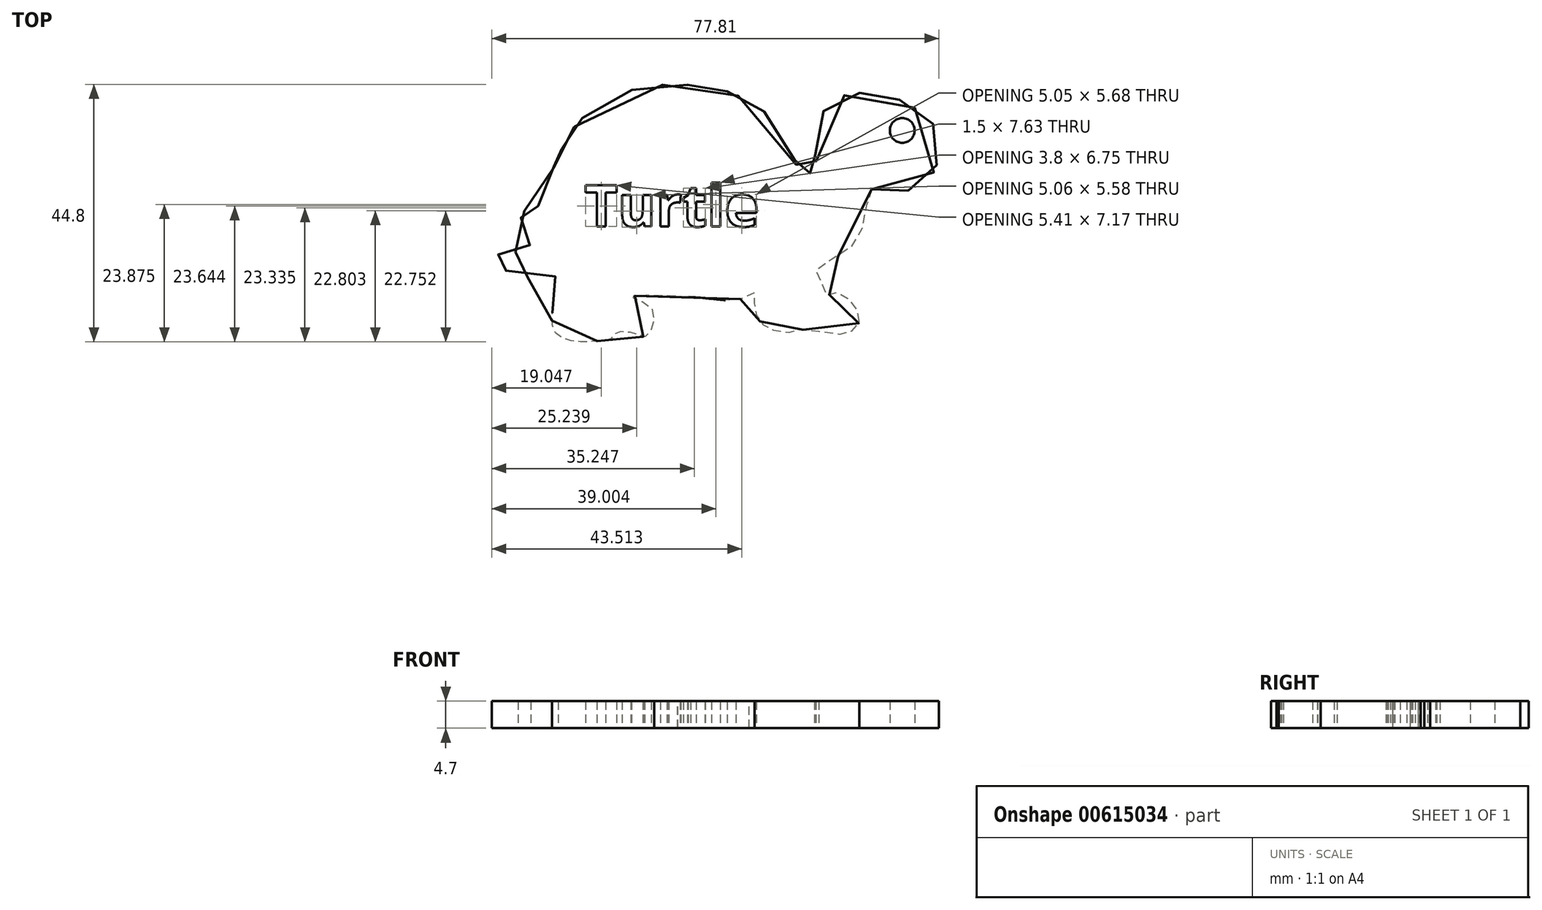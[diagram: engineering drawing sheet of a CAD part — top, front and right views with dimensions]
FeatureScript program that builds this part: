
annotation { "Feature Type Name" : "Feature", "Feature Type Description" : "" }
export const myFeature = defineFeature(function(context is Context, id is Id, definition is map)
    precondition{}
    {
        {
            var Q0;
            Q0=qCreatedBy(makeId("Top.planeOp"),FACE);
            var sketch = newSketch(context, id + "F0", { "sketchPlane" : qUnion([Q0])});
            skFitSpline(sketch, "E0", {"points": [v(-11.52, 31.86) * mm, v(-12.84, 26.48) * mm, v(-16.24, 20.92) * mm, v(-21.24, 17.52) * mm, v(-19.54, 14.32) * mm, v(-19.35, 13.47) * mm, v(-17.66, 13.94) * mm, v(-15.77, 13) * mm, v(-13.88, 10.45) * mm, v(-13.88, 8.37) * mm, v(-15.3, 7.05) * mm, v(-17.84, 6.68) * mm, v(-24.07, 7.43) * mm, v(-25.67, 6.96) * mm, v(-28.7, 7.34) * mm, v(-30.39, 8.28) * mm, v(-31.52, 9.98) * mm, v(-31.9, 12.05) * mm, v(-31.9, 13.84) * mm, v(-34.07, 12.9) * mm, v(-40.1, 12.9) * mm, v(-53.3, 13.18) * mm, v(-49.72, 11.02) * mm, v(-50.67, 6.4) * mm, v(-52.08, 6.58) * mm, v(-55.95, 6.96) * mm, v(-56.99, 5.83) * mm, v(-59.34, 5.45) * mm, v(-62.17, 5.36) * mm, v(-65.85, 6.3) * mm, v(-67.17, 9.41) * mm, v(-66.14, 16.67) * mm, v(-67.74, 16.4) * mm, v(-76.89, 18.66) * mm, v(-77.56, 20.16) * mm, v(-75.76, 20.64) * mm, v(-70.85, 21.86) * mm, v(-72.55, 23.37) * mm, v(-72.55, 26.96) * mm, v(-70.47, 29.5) * mm, v(-69.72, 28.94) * mm, v(-68.02, 32.7) * mm, v(-66.1, 37.5) * mm, v(-66.03, 37.67) * mm, v(-65.82, 38.14) * mm, v(-65.06, 39.76) * mm, v(-62.17, 44.03) * mm, v(-52.74, 49.3) * mm, v(-42.65, 50) * mm, v(-37.37, 49.12) * mm, v(-32.84, 47.14) * mm, v(-26.43, 40.82) * mm, v(-23.6, 33.94) * mm, v(-22.65, 34.69) * mm, v(-20.86, 34.12) * mm, v(-21.33, 37.7) * mm, v(-20.4, 44.69) * mm, v(-16.43, 48.18) * mm, v(-9.73, 48.37) * mm, v(-5.49, 46.86) * mm, v(-0.77, 43.08) * mm, v(0, 37.14) * mm, v(-2.1, 33.18) * mm, v(-8.13, 31.39) * mm, v(-11.52, 31.86) * mm]});
            skText(sketch, "E1", { "text": "Turtle", "fontName": "OpenSans-Bold.ttf"});
            const initialGuessF0  = {"E1": [-0.0615, 0.0254, 1, 0, 0.00723]};
            skSetInitialGuess(sketch, initialGuessF0);
            skSolve(sketch);
        }
        {
            var Q0;
            Q0=makeQuery(id+"F0.imprint","IMPRINT",FACE,{"disambiguationData":[TD([[makeQuery(id+"F0.imprint","IMPRINT",EDGE,{"derivedFrom":sQuery(id+"F0.wireOp",EDGE,"E0")}),-1.0]])]});
            extrude(context, id + "F1", {"entities" : qUnion([Q0]), "depth" : 4.7 * mm, "offsetDistance" : 25 * mm});
        }
        {
            var Q0;
            Q0=qCreatedBy(makeId("Top.planeOp"),FACE);
            var sketch = newSketch(context, id + "F2", { "sketchPlane" : qUnion([Q0])});
            skCircle(sketch, "E2", {"center": v(-6.22, 42.11) * mm, "radius": 2.16 * mm});
            skSolve(sketch);
        }
        {
            var Q0;
            Q0 = qSketchRegion(id + "F2", true);
            var Q1;
            Q1=sQuery(id+"F2.wireOp",EDGE,"E2");
            extrude(context, id + "F3", {"entities" : qUnion([Q0]), "operationType" : NewBodyOperationType.REMOVE, "surfaceEntities" : qUnion([Q1]), "depth" : 5.4 * mm, "offsetDistance" : 25 * mm});
        }
    });
